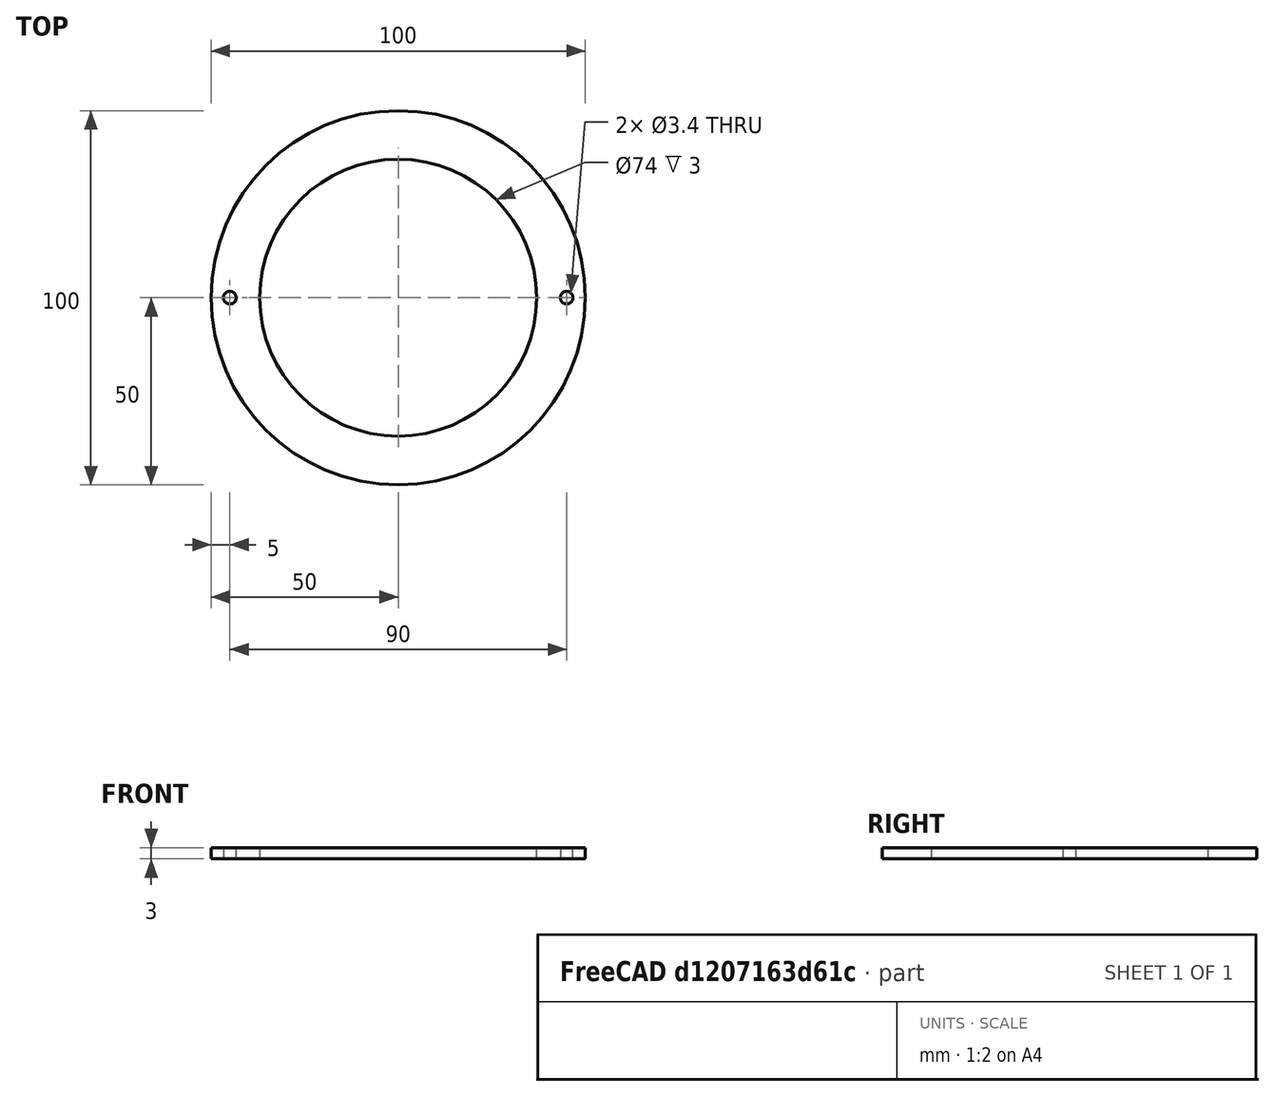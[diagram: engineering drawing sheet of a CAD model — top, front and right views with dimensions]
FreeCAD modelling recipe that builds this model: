
FCSTD DOCUMENT  (FreeCAD 0.19R24291 (Git))
Label: Coiffe-Bot-Lidar
License: All rights reserved
LicenseURL: http://en.wikipedia.org/wiki/All_rights_reserved
objects: Sketcher::SketchObject×1, PartDesign::Pad×1, PartDesign::Body×1
note: 4 computed .brp shape members not serialized (recipe doc carries the construction recipe); baked Part::Feature solids carry a one-line shape summary decoded from their .brp

FEATURE [Sketcher::SketchObject] Sketch
  FullyConstrained = true
  MapMode = 5
  Support = -> [XY_Plane]
  sketch-geometry (6):
    g0: Circle CenterX=0 CenterY=0 CenterZ=0 NormalX=0 NormalY=0 NormalZ=1 AngleXU=0 Radius=50
    g1: Circle CenterX=-45 CenterY=0 CenterZ=0 NormalX=0 NormalY=0 NormalZ=1 AngleXU=0 Radius=1.7
    g2: Circle CenterX=45 CenterY=0 CenterZ=0 NormalX=0 NormalY=0 NormalZ=1 AngleXU=0 Radius=1.7
    g3: GeomPoint X=-50 Y=0 Z=0
    g4: GeomPoint X=50 Y=0 Z=0
    g5: Circle CenterX=0 CenterY=0 CenterZ=0 NormalX=0 NormalY=0 NormalZ=1 AngleXU=0 Radius=37
  constraints (14):
    c: Coincident(g0,g-1)
    c: Radius(g0) = 50
    c: PointOnObject(g1,g-1)
    c: PointOnObject(g2,g-1)
    c: PointOnObject(g3,g-1)
    c: PointOnObject(g4,g-1)
    c: PointOnObject(g4,g0)
    c: PointOnObject(g3,g0)
    c: DistanceX(g3,g1) = 5
    c: DistanceX(g2,g4) = 5
    c: Radius(g2) = 1.7
    c: Equal(g1,g2)
    c: Coincident(g5,g0)
    c: Radius(g5) = 37
FEATURE [PartDesign::Pad] Pad  label="Base"
  Direction = (1,1,1)
  Length = 3
  Length2 = 100
  Profile = -> Sketch
  Type = 0
FEATURE [PartDesign::Body] Body
  Group = -> [Sketch,Pad]
  Origin = -> Origin
  Tip = -> Pad
